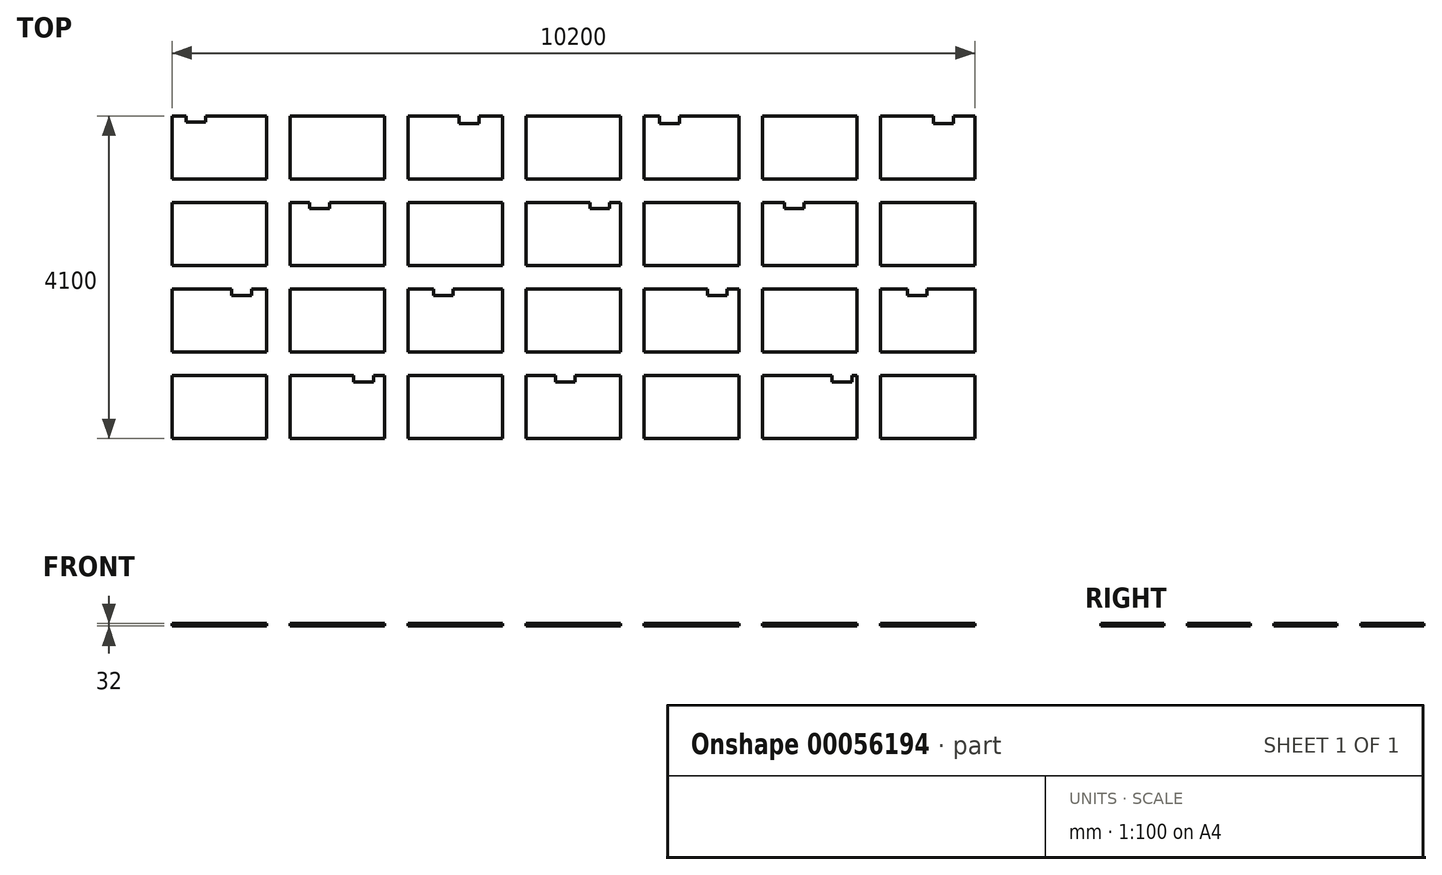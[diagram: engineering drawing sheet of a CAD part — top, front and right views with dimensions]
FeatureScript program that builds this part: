
annotation { "Feature Type Name" : "Feature", "Feature Type Description" : "" }
export const myFeature = defineFeature(function(context is Context, id is Id, definition is map)
    precondition{}
    {
        {
            var Q0;
            Q0=qCreatedBy(makeId("Top.planeOp"),FACE);
            var sketch = newSketch(context, id + "F0", { "sketchPlane" : qUnion([Q0])});
            skLineSegment(sketch, "E0.bottom", {"start": v(-1552.1, 99.4) * mm, "end": v(-1372.1, 99.4) * mm});
            skLineSegment(sketch, "E0.top", {"start": v(-1552.1, -700.6) * mm, "end": v(-352.1, -700.6) * mm});
            skLineSegment(sketch, "E0.left", {"start": v(-1552.1, 99.4) * mm, "end": v(-1552.1, -700.6) * mm});
            skLineSegment(sketch, "E0.right", {"start": v(-352.1, 99.4) * mm, "end": v(-352.1, -700.6) * mm});
            skLineSegment(sketch, "E1.right", {"start": v(1147.9, 99.4) * mm, "end": v(1147.9, -700.6) * mm});
            skLineSegment(sketch, "E1.top", {"start": v(-52.1, -700.6) * mm, "end": v(1147.9, -700.6) * mm});
            skLineSegment(sketch, "E1.bottom", {"start": v(-52.1, 99.4) * mm, "end": v(1147.9, 99.4) * mm});
            skLineSegment(sketch, "E1.left", {"start": v(-52.1, 99.4) * mm, "end": v(-52.1, -700.6) * mm});
            skLineSegment(sketch, "E2.right", {"start": v(2647.9, 99.4) * mm, "end": v(2647.9, -700.6) * mm});
            skLineSegment(sketch, "E2.top", {"start": v(1447.9, -700.6) * mm, "end": v(2647.9, -700.6) * mm});
            skLineSegment(sketch, "E2.bottom", {"start": v(1447.9, 99.4) * mm, "end": v(2097.9, 99.4) * mm});
            skLineSegment(sketch, "E2.left", {"start": v(1447.9, 99.4) * mm, "end": v(1447.9, -700.6) * mm});
            skLineSegment(sketch, "E3.right", {"start": v(4147.9, 99.4) * mm, "end": v(4147.9, -700.6) * mm});
            skLineSegment(sketch, "E3.top", {"start": v(2947.9, -700.6) * mm, "end": v(4147.9, -700.6) * mm});
            skLineSegment(sketch, "E3.bottom", {"start": v(2947.9, 99.4) * mm, "end": v(4147.9, 99.4) * mm});
            skLineSegment(sketch, "E3.left", {"start": v(2947.9, 99.4) * mm, "end": v(2947.9, -700.6) * mm});
            skLineSegment(sketch, "E4.right", {"start": v(5647.9, 99.4) * mm, "end": v(5647.9, -700.6) * mm});
            skLineSegment(sketch, "E4.top", {"start": v(4447.9, -700.6) * mm, "end": v(5647.9, -700.6) * mm});
            skLineSegment(sketch, "E4.bottom", {"start": v(4447.9, 99.4) * mm, "end": v(4642.9, 99.4) * mm});
            skLineSegment(sketch, "E4.left", {"start": v(4447.9, 99.4) * mm, "end": v(4447.9, -700.6) * mm});
            skLineSegment(sketch, "E5.right", {"start": v(7147.9, 99.4) * mm, "end": v(7147.9, -700.6) * mm});
            skLineSegment(sketch, "E5.top", {"start": v(5947.9, -700.6) * mm, "end": v(7147.9, -700.6) * mm});
            skLineSegment(sketch, "E5.bottom", {"start": v(5947.9, 99.4) * mm, "end": v(7147.9, 99.4) * mm});
            skLineSegment(sketch, "E5.left", {"start": v(5947.9, 99.4) * mm, "end": v(5947.9, -700.6) * mm});
            skLineSegment(sketch, "E6.right", {"start": v(8647.9, 99.4) * mm, "end": v(8647.9, -700.6) * mm});
            skLineSegment(sketch, "E6.top", {"start": v(7447.9, -700.6) * mm, "end": v(8647.9, -700.6) * mm});
            skLineSegment(sketch, "E6.bottom", {"start": v(7447.9, 99.4) * mm, "end": v(8122.9, 99.4) * mm});
            skLineSegment(sketch, "E6.left", {"start": v(7447.9, 99.4) * mm, "end": v(7447.9, -700.6) * mm});
            skLineSegment(sketch, "E7.right", {"start": v(-352.1, -1000.6) * mm, "end": v(-352.1, -1800.6) * mm});
            skLineSegment(sketch, "E7.top", {"start": v(-1552.1, -1800.6) * mm, "end": v(-352.1, -1800.6) * mm});
            skLineSegment(sketch, "E7.bottom", {"start": v(-1552.1, -1000.6) * mm, "end": v(-352.1, -1000.6) * mm});
            skLineSegment(sketch, "E7.left", {"start": v(-1552.1, -1000.6) * mm, "end": v(-1552.1, -1800.6) * mm});
            skLineSegment(sketch, "E8.right", {"start": v(1147.9, -1000.6) * mm, "end": v(1147.9, -1800.6) * mm});
            skLineSegment(sketch, "E8.top", {"start": v(-52.1, -1800.6) * mm, "end": v(1147.9, -1800.6) * mm});
            skLineSegment(sketch, "E8.bottom", {"start": v(-52.1, -1000.6) * mm, "end": v(197.9, -1000.6) * mm});
            skLineSegment(sketch, "E8.left", {"start": v(-52.1, -1000.6) * mm, "end": v(-52.1, -1800.6) * mm});
            skLineSegment(sketch, "E9.right", {"start": v(2647.9, -1000.6) * mm, "end": v(2647.9, -1800.6) * mm});
            skLineSegment(sketch, "E9.top", {"start": v(1447.9, -1800.6) * mm, "end": v(2647.9, -1800.6) * mm});
            skLineSegment(sketch, "E9.bottom", {"start": v(1447.9, -1000.6) * mm, "end": v(2647.9, -1000.6) * mm});
            skLineSegment(sketch, "E9.left", {"start": v(1447.9, -1000.6) * mm, "end": v(1447.9, -1800.6) * mm});
            skLineSegment(sketch, "E10.right", {"start": v(4147.9, -1000.6) * mm, "end": v(4147.9, -1800.6) * mm});
            skLineSegment(sketch, "E10.top", {"start": v(2947.9, -1800.6) * mm, "end": v(4147.9, -1800.6) * mm});
            skLineSegment(sketch, "E10.bottom", {"start": v(2947.9, -1000.6) * mm, "end": v(3757.9, -1000.6) * mm});
            skLineSegment(sketch, "E10.left", {"start": v(2947.9, -1000.6) * mm, "end": v(2947.9, -1800.6) * mm});
            skLineSegment(sketch, "E11.right", {"start": v(5647.9, -1000.6) * mm, "end": v(5647.9, -1800.6) * mm});
            skLineSegment(sketch, "E11.top", {"start": v(4447.9, -1800.6) * mm, "end": v(5647.9, -1800.6) * mm});
            skLineSegment(sketch, "E11.bottom", {"start": v(4447.9, -1000.6) * mm, "end": v(5647.9, -1000.6) * mm});
            skLineSegment(sketch, "E11.left", {"start": v(4447.9, -1000.6) * mm, "end": v(4447.9, -1800.6) * mm});
            skLineSegment(sketch, "E12.right", {"start": v(7147.9, -1000.6) * mm, "end": v(7147.9, -1800.6) * mm});
            skLineSegment(sketch, "E12.top", {"start": v(5947.9, -1800.6) * mm, "end": v(7147.9, -1800.6) * mm});
            skLineSegment(sketch, "E12.bottom", {"start": v(5947.9, -1000.6) * mm, "end": v(6227.9, -1000.6) * mm});
            skLineSegment(sketch, "E12.left", {"start": v(5947.9, -1000.6) * mm, "end": v(5947.9, -1800.6) * mm});
            skLineSegment(sketch, "E13.right", {"start": v(8647.9, -1000.6) * mm, "end": v(8647.9, -1800.6) * mm});
            skLineSegment(sketch, "E13.top", {"start": v(7447.9, -1800.6) * mm, "end": v(8647.9, -1800.6) * mm});
            skLineSegment(sketch, "E13.bottom", {"start": v(7447.9, -1000.6) * mm, "end": v(8647.9, -1000.6) * mm});
            skLineSegment(sketch, "E13.left", {"start": v(7447.9, -1000.6) * mm, "end": v(7447.9, -1800.6) * mm});
            skLineSegment(sketch, "E14.right", {"start": v(-352.1, -2100.6) * mm, "end": v(-352.1, -2900.6) * mm});
            skLineSegment(sketch, "E14.top", {"start": v(-1552.1, -2900.6) * mm, "end": v(-352.1, -2900.6) * mm});
            skLineSegment(sketch, "E14.bottom", {"start": v(-1552.1, -2100.6) * mm, "end": v(-792.1, -2100.6) * mm});
            skLineSegment(sketch, "E14.left", {"start": v(-1552.1, -2100.6) * mm, "end": v(-1552.1, -2900.6) * mm});
            skLineSegment(sketch, "E15.right", {"start": v(1147.9, -2100.6) * mm, "end": v(1147.9, -2900.6) * mm});
            skLineSegment(sketch, "E15.top", {"start": v(-52.1, -2900.6) * mm, "end": v(1147.9, -2900.6) * mm});
            skLineSegment(sketch, "E15.bottom", {"start": v(-52.1, -2100.6) * mm, "end": v(1147.9, -2100.6) * mm});
            skLineSegment(sketch, "E15.left", {"start": v(-52.1, -2100.6) * mm, "end": v(-52.1, -2900.6) * mm});
            skLineSegment(sketch, "E16.right", {"start": v(2647.9, -2100.6) * mm, "end": v(2647.9, -2900.6) * mm});
            skLineSegment(sketch, "E16.top", {"start": v(1447.9, -2900.6) * mm, "end": v(2647.9, -2900.6) * mm});
            skLineSegment(sketch, "E16.bottom", {"start": v(1447.9, -2100.6) * mm, "end": v(1767.9, -2100.6) * mm});
            skLineSegment(sketch, "E16.left", {"start": v(1447.9, -2100.6) * mm, "end": v(1447.9, -2900.6) * mm});
            skLineSegment(sketch, "E17.right", {"start": v(4147.9, -2100.6) * mm, "end": v(4147.9, -2900.6) * mm});
            skLineSegment(sketch, "E17.top", {"start": v(2947.9, -2900.6) * mm, "end": v(4147.9, -2900.6) * mm});
            skLineSegment(sketch, "E17.bottom", {"start": v(2947.9, -2100.6) * mm, "end": v(4147.9, -2100.6) * mm});
            skLineSegment(sketch, "E17.left", {"start": v(2947.9, -2100.6) * mm, "end": v(2947.9, -2900.6) * mm});
            skLineSegment(sketch, "E18.right", {"start": v(5647.9, -2100.6) * mm, "end": v(5647.9, -2900.6) * mm});
            skLineSegment(sketch, "E18.top", {"start": v(4447.9, -2900.6) * mm, "end": v(5647.9, -2900.6) * mm});
            skLineSegment(sketch, "E18.bottom", {"start": v(4447.9, -2100.6) * mm, "end": v(5247.9, -2100.6) * mm});
            skLineSegment(sketch, "E18.left", {"start": v(4447.9, -2100.6) * mm, "end": v(4447.9, -2900.6) * mm});
            skLineSegment(sketch, "E19.right", {"start": v(7147.9, -2100.6) * mm, "end": v(7147.9, -2900.6) * mm});
            skLineSegment(sketch, "E19.top", {"start": v(5947.9, -2900.6) * mm, "end": v(7147.9, -2900.6) * mm});
            skLineSegment(sketch, "E19.bottom", {"start": v(5947.9, -2100.6) * mm, "end": v(7147.9, -2100.6) * mm});
            skLineSegment(sketch, "E19.left", {"start": v(5947.9, -2100.6) * mm, "end": v(5947.9, -2900.6) * mm});
            skLineSegment(sketch, "E20.right", {"start": v(8647.9, -2100.6) * mm, "end": v(8647.9, -2900.6) * mm});
            skLineSegment(sketch, "E20.top", {"start": v(7447.9, -2900.6) * mm, "end": v(8647.9, -2900.6) * mm});
            skLineSegment(sketch, "E20.bottom", {"start": v(7447.9, -2100.6) * mm, "end": v(7787.9, -2100.6) * mm});
            skLineSegment(sketch, "E20.left", {"start": v(7447.9, -2100.6) * mm, "end": v(7447.9, -2900.6) * mm});
            skLineSegment(sketch, "E21.right", {"start": v(-352.1, -3200.6) * mm, "end": v(-352.1, -4000.6) * mm});
            skLineSegment(sketch, "E21.top", {"start": v(-1552.1, -4000.6) * mm, "end": v(-352.1, -4000.6) * mm});
            skLineSegment(sketch, "E21.bottom", {"start": v(-1552.1, -3200.6) * mm, "end": v(-352.1, -3200.6) * mm});
            skLineSegment(sketch, "E21.left", {"start": v(-1552.1, -3200.6) * mm, "end": v(-1552.1, -4000.6) * mm});
            skLineSegment(sketch, "E22.right", {"start": v(1147.9, -3200.6) * mm, "end": v(1147.9, -4000.6) * mm});
            skLineSegment(sketch, "E22.top", {"start": v(-52.1, -4000.6) * mm, "end": v(1147.9, -4000.6) * mm});
            skLineSegment(sketch, "E22.bottom", {"start": v(-52.1, -3200.6) * mm, "end": v(757.9, -3200.6) * mm});
            skLineSegment(sketch, "E22.left", {"start": v(-52.1, -3200.6) * mm, "end": v(-52.1, -4000.6) * mm});
            skLineSegment(sketch, "E23.right", {"start": v(2647.9, -3200.6) * mm, "end": v(2647.9, -4000.6) * mm});
            skLineSegment(sketch, "E23.top", {"start": v(1447.9, -4000.6) * mm, "end": v(2647.9, -4000.6) * mm});
            skLineSegment(sketch, "E23.bottom", {"start": v(1447.9, -3200.6) * mm, "end": v(2647.9, -3200.6) * mm});
            skLineSegment(sketch, "E23.left", {"start": v(1447.9, -3200.6) * mm, "end": v(1447.9, -4000.6) * mm});
            skLineSegment(sketch, "E24.right", {"start": v(4147.9, -3200.6) * mm, "end": v(4147.9, -4000.6) * mm});
            skLineSegment(sketch, "E24.top", {"start": v(2947.9, -4000.6) * mm, "end": v(4147.9, -4000.6) * mm});
            skLineSegment(sketch, "E24.bottom", {"start": v(2947.9, -3200.6) * mm, "end": v(3317.9, -3200.6) * mm});
            skLineSegment(sketch, "E24.left", {"start": v(2947.9, -3200.6) * mm, "end": v(2947.9, -4000.6) * mm});
            skLineSegment(sketch, "E25.right", {"start": v(5647.9, -3200.6) * mm, "end": v(5647.9, -4000.6) * mm});
            skLineSegment(sketch, "E25.top", {"start": v(4447.9, -4000.6) * mm, "end": v(5647.9, -4000.6) * mm});
            skLineSegment(sketch, "E25.bottom", {"start": v(4447.9, -3200.6) * mm, "end": v(5647.9, -3200.6) * mm});
            skLineSegment(sketch, "E25.left", {"start": v(4447.9, -3200.6) * mm, "end": v(4447.9, -4000.6) * mm});
            skLineSegment(sketch, "E26.right", {"start": v(7147.9, -3200.6) * mm, "end": v(7147.9, -4000.6) * mm});
            skLineSegment(sketch, "E26.top", {"start": v(5947.9, -4000.6) * mm, "end": v(7147.9, -4000.6) * mm});
            skLineSegment(sketch, "E26.bottom", {"start": v(5947.9, -3200.6) * mm, "end": v(6832.9, -3200.6) * mm});
            skLineSegment(sketch, "E26.left", {"start": v(5947.9, -3200.6) * mm, "end": v(5947.9, -4000.6) * mm});
            skLineSegment(sketch, "E27.right", {"start": v(8647.9, -3200.6) * mm, "end": v(8647.9, -4000.6) * mm});
            skLineSegment(sketch, "E27.top", {"start": v(7447.9, -4000.6) * mm, "end": v(8647.9, -4000.6) * mm});
            skLineSegment(sketch, "E27.bottom", {"start": v(7447.9, -3200.6) * mm, "end": v(8647.9, -3200.6) * mm});
            skLineSegment(sketch, "E27.left", {"start": v(7447.9, -3200.6) * mm, "end": v(7447.9, -4000.6) * mm});
            skLineSegment(sketch, "E28.top", {"start": v(-1372.1, 19.4) * mm, "end": v(-1122.1, 19.4) * mm});
            skLineSegment(sketch, "E28.left", {"start": v(-1372.1, 99.4) * mm, "end": v(-1372.1, 19.4) * mm});
            skLineSegment(sketch, "E28.right", {"start": v(-1122.1, 99.4) * mm, "end": v(-1122.1, 19.4) * mm});
            skLineSegment(sketch, "E29.trimOffspring", {"start": v(-1122.1, 99.4) * mm, "end": v(-352.1, 99.4) * mm});
            skLineSegment(sketch, "E30.top", {"start": v(2097.9, 0) * mm, "end": v(2347.9, 0) * mm});
            skLineSegment(sketch, "E30.left", {"start": v(2097.9, 99.4) * mm, "end": v(2097.9, 0) * mm});
            skLineSegment(sketch, "E30.right", {"start": v(2347.9, 99.4) * mm, "end": v(2347.9, 0) * mm});
            skLineSegment(sketch, "E31.trimOffspring", {"start": v(2347.9, 99.4) * mm, "end": v(2647.9, 99.4) * mm});
            skLineSegment(sketch, "E32.top", {"start": v(4642.9, 0) * mm, "end": v(4892.9, 0) * mm});
            skLineSegment(sketch, "E32.left", {"start": v(4642.9, 99.4) * mm, "end": v(4642.9, 0) * mm});
            skLineSegment(sketch, "E32.right", {"start": v(4892.9, 99.4) * mm, "end": v(4892.9, 0) * mm});
            skLineSegment(sketch, "E33.trimOffspring", {"start": v(4892.9, 99.4) * mm, "end": v(5647.9, 99.4) * mm});
            skLineSegment(sketch, "E34.top", {"start": v(8122.9, 0) * mm, "end": v(8372.9, 0) * mm});
            skLineSegment(sketch, "E34.left", {"start": v(8122.9, 99.4) * mm, "end": v(8122.9, 0) * mm});
            skLineSegment(sketch, "E34.right", {"start": v(8372.9, 99.4) * mm, "end": v(8372.9, 0) * mm});
            skLineSegment(sketch, "E35.trimOffspring", {"start": v(8372.9, 99.4) * mm, "end": v(8647.9, 99.4) * mm});
            skLineSegment(sketch, "E36.top", {"start": v(197.9, -1080.6) * mm, "end": v(447.9, -1080.6) * mm});
            skLineSegment(sketch, "E36.left", {"start": v(197.9, -1000.6) * mm, "end": v(197.9, -1080.6) * mm});
            skLineSegment(sketch, "E36.right", {"start": v(447.9, -1000.6) * mm, "end": v(447.9, -1080.6) * mm});
            skLineSegment(sketch, "E37.trimOffspring", {"start": v(447.9, -1000.6) * mm, "end": v(1147.9, -1000.6) * mm});
            skLineSegment(sketch, "E38.top", {"start": v(3757.9, -1080.6) * mm, "end": v(4007.9, -1080.6) * mm});
            skLineSegment(sketch, "E38.left", {"start": v(3757.9, -1000.6) * mm, "end": v(3757.9, -1080.6) * mm});
            skLineSegment(sketch, "E38.right", {"start": v(4007.9, -1000.6) * mm, "end": v(4007.9, -1080.6) * mm});
            skLineSegment(sketch, "E39.trimOffspring", {"start": v(4007.9, -1000.6) * mm, "end": v(4147.9, -1000.6) * mm});
            skLineSegment(sketch, "E40.top", {"start": v(6227.9, -1080.6) * mm, "end": v(6477.9, -1080.6) * mm});
            skLineSegment(sketch, "E40.left", {"start": v(6227.9, -1000.6) * mm, "end": v(6227.9, -1080.6) * mm});
            skLineSegment(sketch, "E40.right", {"start": v(6477.9, -1000.6) * mm, "end": v(6477.9, -1080.6) * mm});
            skLineSegment(sketch, "E41.trimOffspring", {"start": v(6477.9, -1000.6) * mm, "end": v(7147.9, -1000.6) * mm});
            skLineSegment(sketch, "E42.top", {"start": v(-792.1, -2180.6) * mm, "end": v(-542.1, -2180.6) * mm});
            skLineSegment(sketch, "E42.left", {"start": v(-792.1, -2100.6) * mm, "end": v(-792.1, -2180.6) * mm});
            skLineSegment(sketch, "E42.right", {"start": v(-542.1, -2100.6) * mm, "end": v(-542.1, -2180.6) * mm});
            skLineSegment(sketch, "E43.trimOffspring", {"start": v(-542.1, -2100.6) * mm, "end": v(-352.1, -2100.6) * mm});
            skLineSegment(sketch, "E44.top", {"start": v(1767.9, -2180.6) * mm, "end": v(2017.9, -2180.6) * mm});
            skLineSegment(sketch, "E44.left", {"start": v(1767.9, -2100.6) * mm, "end": v(1767.9, -2180.6) * mm});
            skLineSegment(sketch, "E44.right", {"start": v(2017.9, -2100.6) * mm, "end": v(2017.9, -2180.6) * mm});
            skLineSegment(sketch, "E45.trimOffspring", {"start": v(2017.9, -2100.6) * mm, "end": v(2647.9, -2100.6) * mm});
            skLineSegment(sketch, "E46.top", {"start": v(5247.9, -2180.6) * mm, "end": v(5497.9, -2180.6) * mm});
            skLineSegment(sketch, "E46.left", {"start": v(5247.9, -2100.6) * mm, "end": v(5247.9, -2180.6) * mm});
            skLineSegment(sketch, "E46.right", {"start": v(5497.9, -2100.6) * mm, "end": v(5497.9, -2180.6) * mm});
            skLineSegment(sketch, "E47.trimOffspring", {"start": v(5497.9, -2100.6) * mm, "end": v(5647.9, -2100.6) * mm});
            skLineSegment(sketch, "E48.top", {"start": v(7787.9, -2180.6) * mm, "end": v(8037.9, -2180.6) * mm});
            skLineSegment(sketch, "E48.left", {"start": v(7787.9, -2100.6) * mm, "end": v(7787.9, -2180.6) * mm});
            skLineSegment(sketch, "E48.right", {"start": v(8037.9, -2100.6) * mm, "end": v(8037.9, -2180.6) * mm});
            skLineSegment(sketch, "E49.trimOffspring", {"start": v(8037.9, -2100.6) * mm, "end": v(8647.9, -2100.6) * mm});
            skLineSegment(sketch, "E50.top", {"start": v(757.9, -3280.6) * mm, "end": v(1007.9, -3280.6) * mm});
            skLineSegment(sketch, "E50.left", {"start": v(757.9, -3200.6) * mm, "end": v(757.9, -3280.6) * mm});
            skLineSegment(sketch, "E50.right", {"start": v(1007.9, -3200.6) * mm, "end": v(1007.9, -3280.6) * mm});
            skLineSegment(sketch, "E51.trimOffspring", {"start": v(1007.9, -3200.6) * mm, "end": v(1147.9, -3200.6) * mm});
            skLineSegment(sketch, "E52.top", {"start": v(3317.9, -3280.6) * mm, "end": v(3567.9, -3280.6) * mm});
            skLineSegment(sketch, "E52.left", {"start": v(3317.9, -3200.6) * mm, "end": v(3317.9, -3280.6) * mm});
            skLineSegment(sketch, "E52.right", {"start": v(3567.9, -3200.6) * mm, "end": v(3567.9, -3280.6) * mm});
            skLineSegment(sketch, "E53.trimOffspring", {"start": v(3567.9, -3200.6) * mm, "end": v(4147.9, -3200.6) * mm});
            skLineSegment(sketch, "E54.top", {"start": v(6832.9, -3280.6) * mm, "end": v(7082.9, -3280.6) * mm});
            skLineSegment(sketch, "E54.left", {"start": v(6832.9, -3200.6) * mm, "end": v(6832.9, -3280.6) * mm});
            skLineSegment(sketch, "E54.right", {"start": v(7082.9, -3200.6) * mm, "end": v(7082.9, -3280.6) * mm});
            skLineSegment(sketch, "E55.trimOffspring", {"start": v(7082.9, -3200.6) * mm, "end": v(7147.9, -3200.6) * mm});
            skSolve(sketch);
        }
        {
            var Q0;
            Q0 = qSketchRegion(id + "F0", true);
            extrude(context, id + "F1", {"entities" : qUnion([Q0]), "depth" : 32 * mm});
        }
    });
